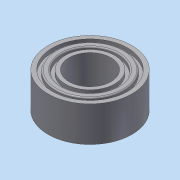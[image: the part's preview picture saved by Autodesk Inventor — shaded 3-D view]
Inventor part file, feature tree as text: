
AUTODESK INVENTOR PART (.ipt)
format: ipt  version: 2013 (Build 170138000, 138)  size: 171,008 bytes
history: native  units: mm
features: extrude x2, fillet x2, sketch x2, mirror x1
ambient origin geometry x8: Origin, YZ Plane, XZ Plane, XY Plane, X Axis, Y Axis, Z Axis, Center Point
bodies: Solid1 (feature_tree)
feature tree (7):
  extrude  "Extrusion1"  Depth=5.0mm
  extrude  "Extrusion2"  Depth=0.5mm
  fillet  "Fillet1"  Radius=0.4mm
  mirror  "Mirror1"
  fillet  "Fillet2"  Radius=0.75mm
  sketch  "Sketch1"  dims[d0=10.0mm d1=5.0mm]
  sketch  "Sketch2"  dims[d2=4.2mm d3=0.0mm d4=0.5mm d5=0.4mm d6=0.75mm d7=0.4mm d8=0.5mm d9=0.0mm d10=0.15mm d11=0.15mm]
